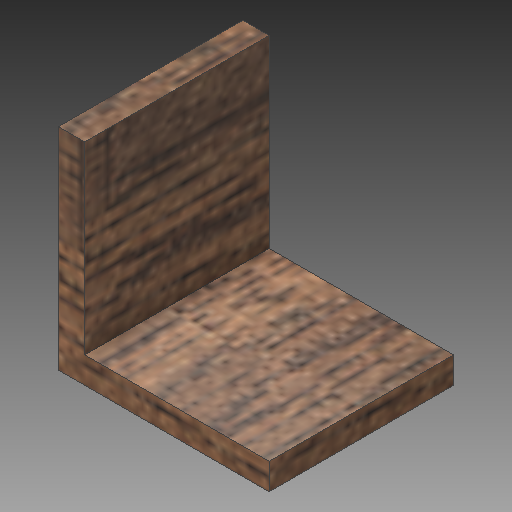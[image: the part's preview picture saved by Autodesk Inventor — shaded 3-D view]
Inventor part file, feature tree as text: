
AUTODESK INVENTOR PART (.ipt)
format: ipt  version: 2017 (Build 210142000, 142)  size: 293,376 bytes
history: native  units: in
note: dims shown in document units (in); Inventor stores cm internally (conversion verified against a paired STEP export)
features: extrude x2, sketch x2
ambient origin geometry x8: Origin, YZ Plane, XZ Plane, XY Plane, X Axis, Y Axis, Z Axis, Center Point
bodies: Solid1 (feature_tree)
feature tree (4):
  extrude  "Extrusion1"  Depth=4.0in
  extrude  "Extrusion2"  Depth=0.5in
  sketch  "Sketch1"  dims[d0=3.5in d1=4.0in]
  sketch  "Sketch2"  dims[d2=0.5in d3=0.0in d4=0.5in d5=3.5in d6=0.0in]
